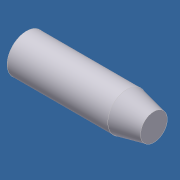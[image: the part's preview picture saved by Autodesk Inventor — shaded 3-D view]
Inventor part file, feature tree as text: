
AUTODESK INVENTOR PART (.ipt)
format: ipt  version: unknown  size: 160,768 bytes
history: native  units: in
note: dims shown in document units (in); Inventor stores cm internally (conversion verified against a paired STEP export)
features: revolve x1, sketch x1
ambient origin geometry x8: Origin, YZ Plane, XZ Plane, XY Plane, X Axis, Y Axis, Z Axis, Center Point
feature tree (2):
  revolve  "Revolution1"  Angle=90.0deg
  sketch  "Sketch1"  dims[d2=4.75in d4=90.0deg d5=0.7188in d6=0.5in d7=1.0in]
